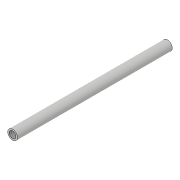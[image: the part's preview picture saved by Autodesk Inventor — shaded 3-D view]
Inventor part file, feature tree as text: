
AUTODESK INVENTOR PART (.ipt)
format: ipt  version: 2018.3 (Build 223284000, 284)  size: 83,968 bytes
history: native  units: in
note: dims shown in document units (in); Inventor stores cm internally (conversion verified against a paired STEP export)
features: sketch x3, hole x2, extrude x1
ambient origin geometry x8: Origin, YZ Plane, XZ Plane, XY Plane, X Axis, Y Axis, Z Axis, Center Point
bodies: Solid1 (feature_tree)
feature tree (6):
  extrude  "Extrusion1"  Depth=3.0in TaperAngle=0.0deg
  hole  "Hole1"  [1 undecoded]
  hole  "Hole2"  [1 undecoded]
  sketch  "Sketch1"  dims[d0=0.1875in d1=3.0in d2=0.0in]
  sketch  "Sketch2"  dims[d3=0.089in]
  sketch  "Sketch3"  dims[d4=0.13in d5=0.328in d6=0.375in d7=0.25in d8=0.5635in d9=0.484in d10=0.8108in d11=0.13in d12=0.328in d13=0.375in d14=0.25in d15=0.5635in d16=0.484in d17=0.8108in]
note: 2 required parameter values undecoded (feature->parameter linkage not recoverable at this tier; creation-order binding heuristic only, values carry confidence <= 0.55)
